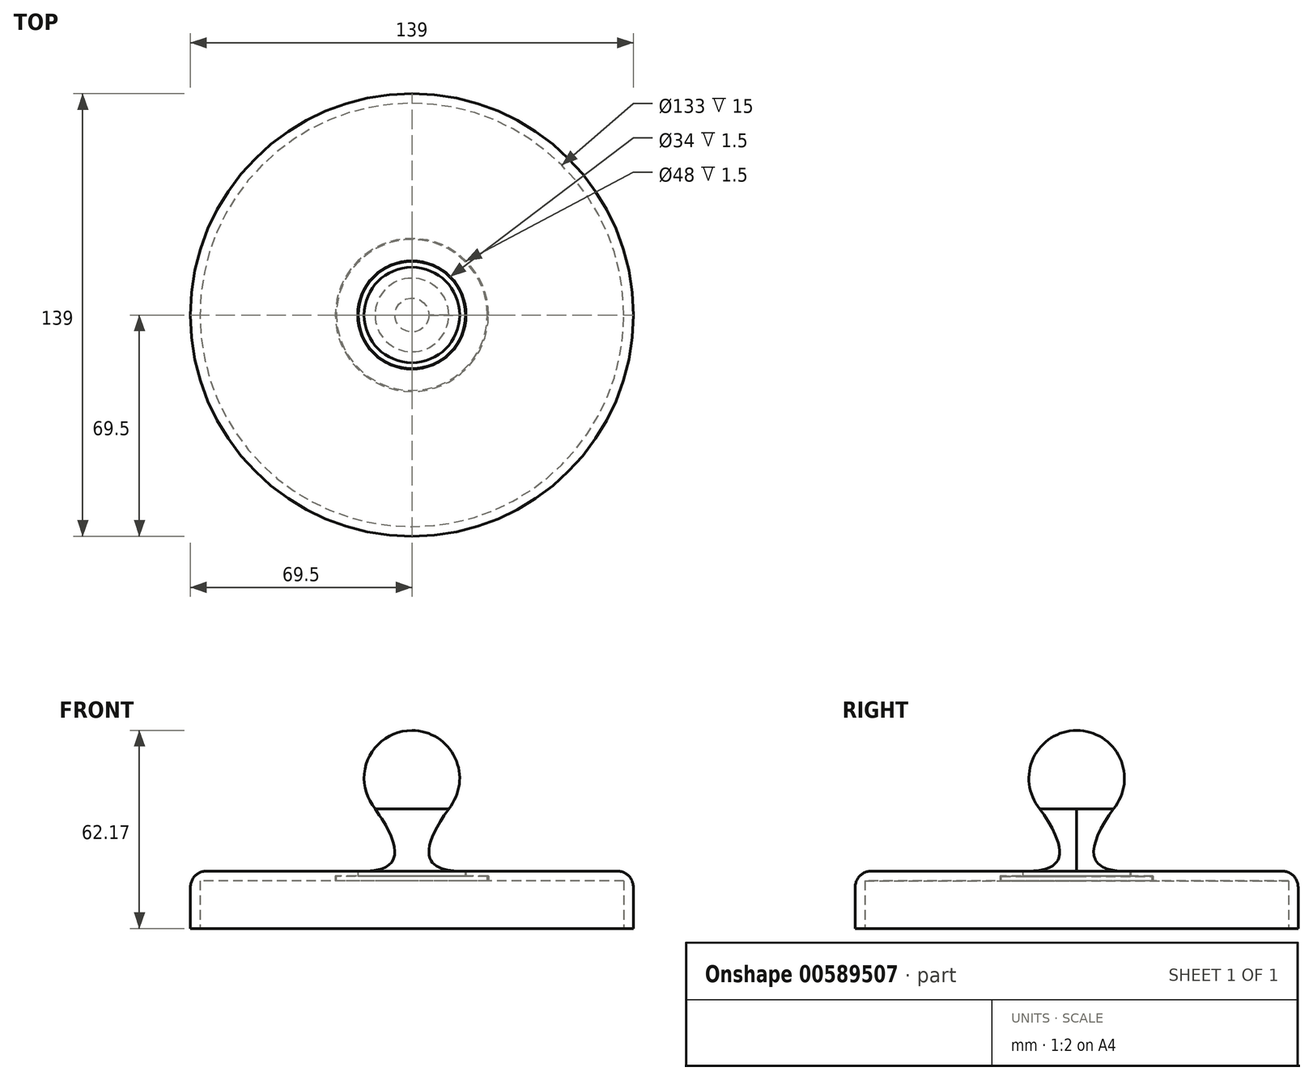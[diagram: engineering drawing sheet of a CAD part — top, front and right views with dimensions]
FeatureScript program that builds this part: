
annotation { "Feature Type Name" : "Feature", "Feature Type Description" : "" }
export const myFeature = defineFeature(function(context is Context, id is Id, definition is map)
    precondition{}
    {
        {
            var Q0;
            Q0=qCreatedBy(makeId("Top.planeOp"),FACE);
            var sketch = newSketch(context, id + "F0", { "sketchPlane" : qUnion([Q0])});
            skCircle(sketch, "E0", {"center": v(0, 0) * mm, "radius": 66.5 * mm});
            skCircle(sketch, "E1.0", {"center": v(0, 0) * mm, "radius": 69.5 * mm});
            skSolve(sketch);
        }
        {
            var Q0;
            Q0=makeQuery(id+"F0.imprint","IMPRINT",FACE,{"disambiguationData":[TD([[makeQuery(id+"F0.imprint","IMPRINT",EDGE,{"derivedFrom":sQuery(id+"F0.wireOp",EDGE,"E0")}),-1.0]])]});
            var Q1;
            Q1=makeQuery(id+"F0.imprint","IMPRINT",FACE,{"disambiguationData":[TD([[makeQuery(id+"F0.imprint","IMPRINT",EDGE,{"derivedFrom":sQuery(id+"F0.wireOp",EDGE,"E0")}),1.0]])]});
            extrude(context, id + "F1", {"entities" : qUnion([Q0, Q1]), "depth" : 18 * mm, "offsetDistance" : 25 * mm});
        }
        {
            var Q0;
            Q0=makeQuery(id+"F0.imprint","IMPRINT",FACE,{"disambiguationData":[TD([[makeQuery(id+"F0.imprint","IMPRINT",EDGE,{"derivedFrom":sQuery(id+"F0.wireOp",EDGE,"E0")}),1.0]])]});
            extrude(context, id + "F2", {"entities" : qUnion([Q0]), "operationType" : NewBodyOperationType.REMOVE, "depth" : 15 * mm, "offsetDistance" : 25 * mm});
        }
        {
            var Q0;
            Q0=makeQuery(id+"F1.opExtrude","CAP_FACE",FACE,{"disambiguationData":[OSD([sQuery(id+"F0.wireOp",EDGE,"E1.0")])],"isStart":false});
            fillet(context, id + "F3", {"entities" : qUnion([Q0]), "radius" : 5 * mm, "tangentPropagation" : true, "allowEdgeOverflow" : false});
        }
        {
            var Q0;
            Q0=qCreatedBy(makeId("Top.planeOp"),FACE);
            var sketch = newSketch(context, id + "F4", { "sketchPlane" : qUnion([Q0])});
            skCircle(sketch, "E2", {"center": v(0, 0) * mm, "radius": 17 * mm});
            skCircle(sketch, "E3", {"center": v(0, 0) * mm, "radius": 24 * mm});
            skSolve(sketch);
        }
        {
            var Q0;
            Q0=makeQuery(id+"F4.imprint","IMPRINT",FACE,{"disambiguationData":[TD([[makeQuery(id+"F4.imprint","IMPRINT",EDGE,{"derivedFrom":sQuery(id+"F4.wireOp",EDGE,"E2")}),1.0]])]});
            extrude(context, id + "F5", {"entities" : qUnion([Q0]), "operationType" : NewBodyOperationType.REMOVE, "endBound" : BoundingType.THROUGH_ALL, "depth" : 25 * mm, "offsetDistance" : 25 * mm});
        }
        {
            var Q0;
            Q0=makeQuery(id+"F4.imprint","IMPRINT",FACE,{"disambiguationData":[TD([[makeQuery(id+"F4.imprint","IMPRINT",EDGE,{"derivedFrom":sQuery(id+"F4.wireOp",EDGE,"E2")}),-1.0]])]});
            extrude(context, id + "F6", {"entities" : qUnion([Q0]), "operationType" : NewBodyOperationType.REMOVE, "depth" : 16.5 * mm, "offsetDistance" : 25 * mm});
        }
        {
            var Q0;
            Q0=qCreatedBy(makeId("Front.planeOp"),FACE);
            var sketch = newSketch(context, id + "F7", { "sketchPlane" : qUnion([Q0])});
            skArc(sketch, "E4", {"start": v(0, 62.17) * mm, "mid": v(-15, 47.17) * mm, "end": v(0, 32.17) * mm});
            skLineSegment(sketch, "E5", {"start": v(0, 62.17) * mm, "end": v(0, 14.52) * mm});
            skLineSegment(sketch, "E6", {"start": v(-15.44, 18) * mm, "end": v(0, 18) * mm});
            skFitSpline(sketch, "E7", {"points": [v(-11.56, 37.6) * mm, v(-15.44, 18) * mm], "startDerivative": vector(34.67, -48.88) * mm, "endDerivative": vector(-26.76, 0) * mm});
            skLineSegment(sketch, "E8", {"start": v(-15.44, 18) * mm, "end": v(-16.85, 18) * mm});
            skLineSegment(sketch, "E9", {"start": v(-16.85, 18) * mm, "end": v(-16.85, 16.35) * mm});
            skLineSegment(sketch, "E10", {"start": v(-16.85, 16.35) * mm, "end": v(-23.7, 16.35) * mm});
            skLineSegment(sketch, "E11", {"start": v(-23.7, 16.35) * mm, "end": v(-23.7, 15) * mm});
            skLineSegment(sketch, "E12", {"start": v(-23.7, 15) * mm, "end": v(0, 15) * mm});
            skSolve(sketch);
        }
        {
            var Q0;
            {var subQ0=sQuery(id+"F7.wireOp",EDGE,"E5");var subQ1=sQuery(id+"F7.wireOp",EDGE,"E4");var subQ2=makeQuery(id+"F7.imprint","INTERSECT",VERTEX,{"disambiguationData":[OD(0.0)],"derivedFrom":[subQ1,subQ0]});Q0=makeQuery(id+"F7.imprint","IMPRINT",FACE,{"disambiguationData":[TD([[makeQuery(id+"F7.imprint","IMPRINT",EDGE,{"disambiguationData":[TD([[subQ2,-1.0]])],"derivedFrom":subQ1}),1.0]])]});}
            var Q1;
            {var subQ4=sQuery(id+"F7.wireOp",EDGE,"E6");Q1=makeQuery(id+"F7.imprint","IMPRINT",FACE,{"disambiguationData":[TD([[makeQuery(id+"F7.imprint","IMPRINT",EDGE,{"derivedFrom":subQ4}),1.0]])]});}
            var Q2;
            {var subQ0=sQuery(id+"F7.wireOp",EDGE,"E6");Q2=makeQuery(id+"F7.imprint","IMPRINT",FACE,{"disambiguationData":[TD([[makeQuery(id+"F7.imprint","IMPRINT",EDGE,{"derivedFrom":subQ0}),-1.0]])]});}
            var Q3;
            Q3=sQuery(id+"F7.wireOp",EDGE,"E5");
            revolve(context, id + "F8", {"entities" : qUnion([Q0, Q1, Q2]), "axis" : qUnion([Q3]), "revolveType" : RevolveType.FULL});
        }
    });
